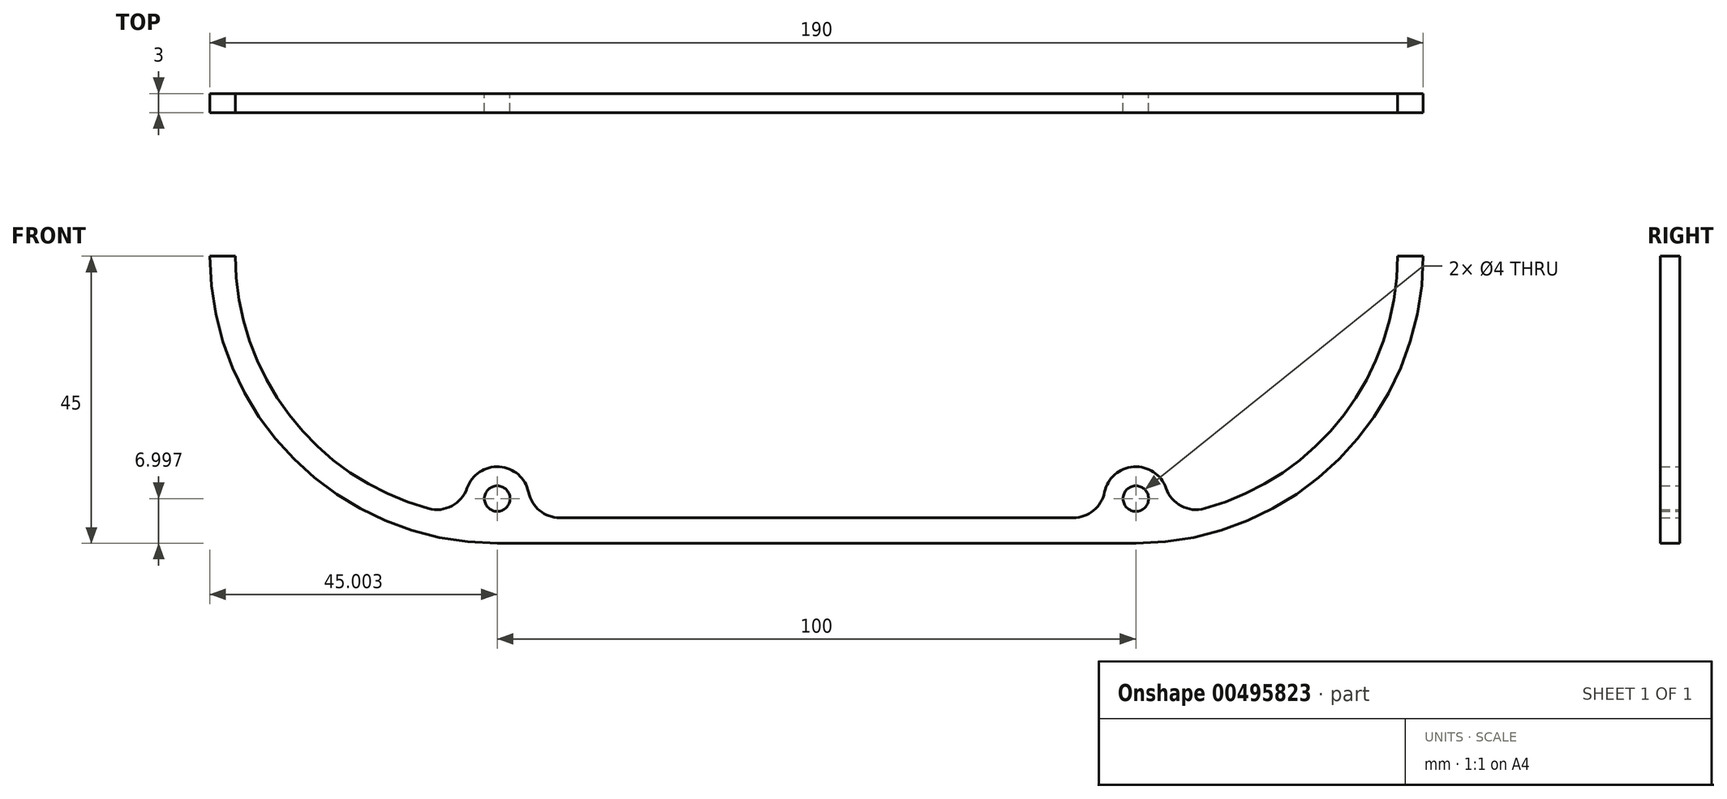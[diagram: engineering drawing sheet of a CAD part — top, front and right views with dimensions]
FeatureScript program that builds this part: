
annotation { "Feature Type Name" : "Feature", "Feature Type Description" : "" }
export const myFeature = defineFeature(function(context is Context, id is Id, definition is map)
    precondition{}
    {
        {
            var Q0;
            Q0=qCreatedBy(makeId("Front.planeOp"),FACE);
            var sketch = newSketch(context, id + "F0", { "sketchPlane" : qUnion([Q0])});
            skArc(sketch, "E0.0", {"start": v(-158.78, 73.57) * mm, "mid": v(-145.6, 41.75) * mm, "end": v(-113.78, 28.57) * mm});
            skArc(sketch, "E0.2", {"start": v(-13.78, 28.57) * mm, "mid": v(18.04, 41.75) * mm, "end": v(31.22, 73.57) * mm});
            skLineSegment(sketch, "E0.3", {"start": v(-113.78, 28.57) * mm, "end": v(-13.78, 28.57) * mm});
            skArc(sketch, "E1.1", {"start": v(-154.78, 73.57) * mm, "mid": v(-146.35, 48.67) * mm, "end": v(-124.54, 34) * mm});
            skArc(sketch, "E1.3", {"start": v(-118.5, 37.2) * mm, "mid": v(-113.45, 40.56) * mm, "end": v(-108.88, 36.57) * mm});
            skArc(sketch, "E1.5", {"start": v(27.22, 73.57) * mm, "mid": v(18.8, 48.67) * mm, "end": v(-3.01, 34) * mm});
            skArc(sketch, "E1.6", {"start": v(-9.05, 37.2) * mm, "mid": v(-14.1, 40.56) * mm, "end": v(-18.68, 36.57) * mm});
            skLineSegment(sketch, "E1.7", {"start": v(-23.58, 32.57) * mm, "end": v(-103.98, 32.57) * mm});
            skCircle(sketch, "E2.0", {"center": v(-13.78, 35.57) * mm, "radius": 2 * mm});
            skCircle(sketch, "E3.0", {"center": v(-113.78, 35.57) * mm, "radius": 2 * mm});
            skPoint(sketch, "E4.visualSharp", {"position": v(-109.78, 114.57) * mm});
            skPoint(sketch, "E5.visualSharp", {"position": v(-117.93, 114.36) * mm});
            skPoint(sketch, "E6.visualSharp", {"position": v(-17.78, 114.57) * mm});
            skPoint(sketch, "E7.visualSharp", {"position": v(-9.63, 114.36) * mm});
            skPoint(sketch, "E8.visualSharp", {"position": v(-9.63, 32.78) * mm});
            skArc(sketch, "E8.filletArc", {"start": v(-9.05, 37.2) * mm, "mid": v(-6.66, 34.41) * mm, "end": v(-3.01, 34) * mm});
            skPoint(sketch, "E9.visualSharp", {"position": v(-17.78, 32.57) * mm});
            skArc(sketch, "E9.filletArc", {"start": v(-23.58, 32.57) * mm, "mid": v(-20.41, 33.7) * mm, "end": v(-18.68, 36.57) * mm});
            skPoint(sketch, "E10.visualSharp", {"position": v(-109.78, 32.57) * mm});
            skArc(sketch, "E10.filletArc", {"start": v(-108.88, 36.57) * mm, "mid": v(-107.14, 33.7) * mm, "end": v(-103.98, 32.57) * mm});
            skPoint(sketch, "E11.visualSharp", {"position": v(-117.93, 32.78) * mm});
            skArc(sketch, "E11.filletArc", {"start": v(-124.54, 34) * mm, "mid": v(-120.9, 34.41) * mm, "end": v(-118.5, 37.2) * mm});
            skLineSegment(sketch, "E12", {"start": v(-154.78, 73.57) * mm, "end": v(-158.78, 73.57) * mm});
            skLineSegment(sketch, "E13", {"start": v(-158.78, 73.57) * mm, "end": v(-154.78, 73.57) * mm});
            skLineSegment(sketch, "E14.trimOffspring", {"start": v(27.22, 73.57) * mm, "end": v(31.22, 73.57) * mm});
            skSolve(sketch);
        }
        {
            var Q0;
            Q0 = qSketchRegion(id + "F0", true);
            extrude(context, id + "F1", {"entities" : qUnion([Q0]), "depth" : 3 * mm, "offsetDistance" : 25 * mm});
        }
    });
